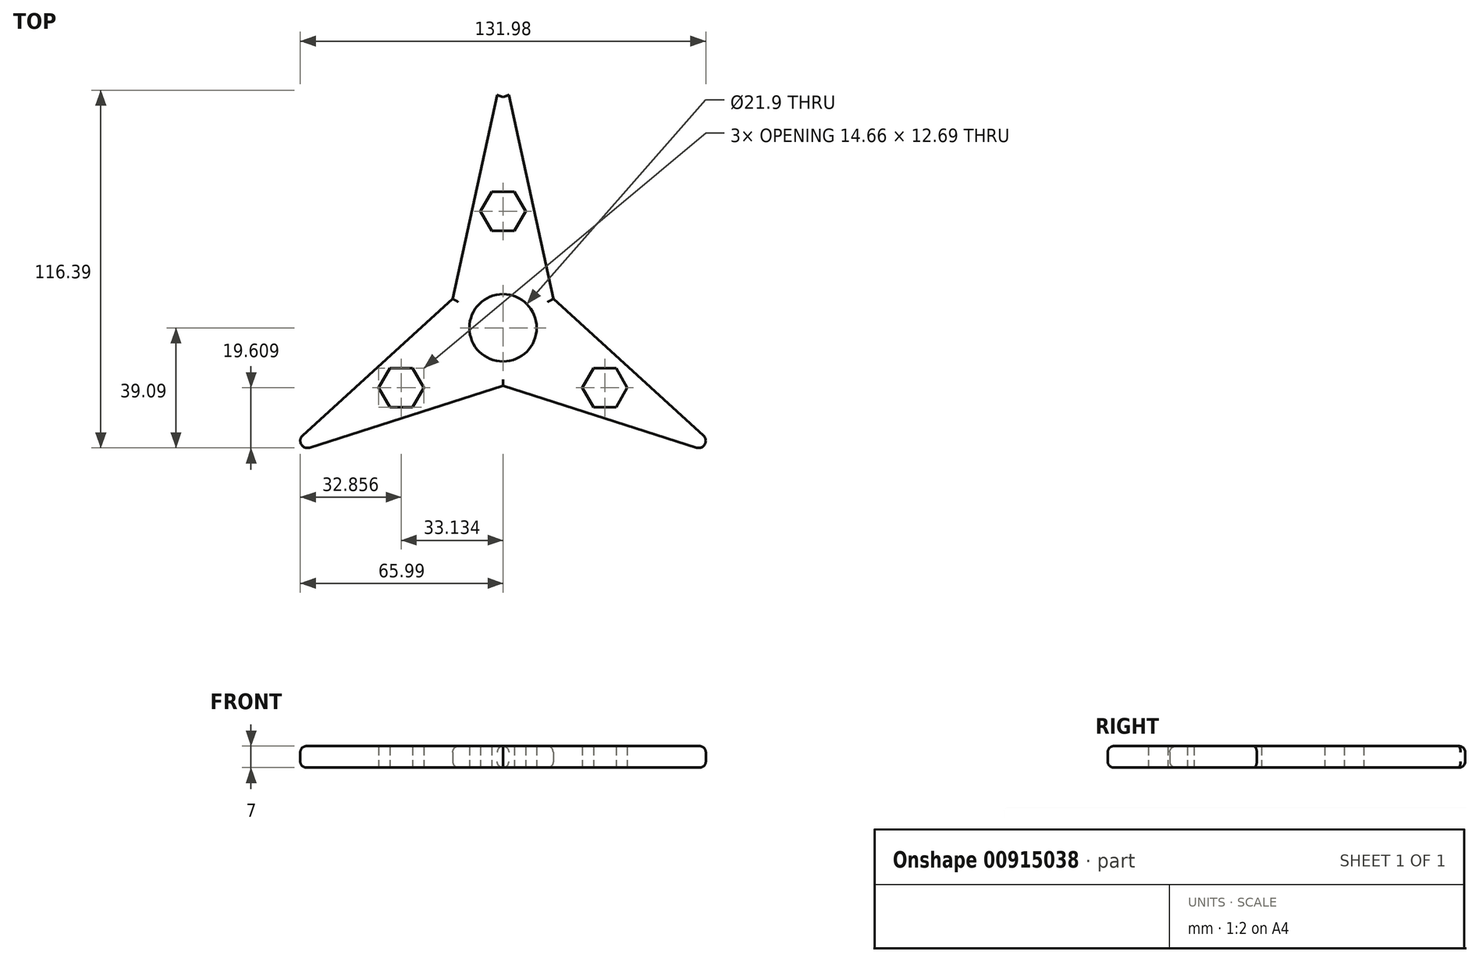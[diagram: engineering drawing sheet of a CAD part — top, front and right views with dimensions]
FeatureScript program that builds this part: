
annotation { "Feature Type Name" : "Feature", "Feature Type Description" : "" }
export const myFeature = defineFeature(function(context is Context, id is Id, definition is map)
    precondition{}
    {
        {
            var Q0;
            Q0=qCreatedBy(makeId("Top.planeOp"),FACE);
            var sketch = newSketch(context, id + "F0", { "sketchPlane" : qUnion([Q0])});
            skLineSegment(sketch, "E0", {"start": v(16.35, 9.44) * mm, "end": v(1.89, 75.78) * mm});
            skLineSegment(sketch, "E1", {"start": v(-1.89, 75.78) * mm, "end": v(-16.35, 9.44) * mm});
            skLineSegment(sketch, "E2.1.0", {"start": v(-62.96, -38.98) * mm, "end": v(0, -18.88) * mm});
            skLineSegment(sketch, "E2.1.1", {"start": v(-16.35, 9.44) * mm, "end": v(-65.23, -35.03) * mm});
            skLineSegment(sketch, "E2.2.0", {"start": v(65.23, -35.03) * mm, "end": v(16.35, 9.44) * mm});
            skLineSegment(sketch, "E2.2.1", {"start": v(0, -18.88) * mm, "end": v(62.96, -38.98) * mm});
            skCircle(sketch, "E3", {"center": v(0, 0) * mm, "radius": 10.95 * mm});
            skCircle(sketch, "E4.cCircle", {"center": v(0, 37.9) * mm, "radius": 6.35 * mm, "construction": true});
            skLineSegment(sketch, "E4.0", {"start": v(3.66, 31.56) * mm, "end": v(-3.66, 31.56) * mm});
            skLineSegment(sketch, "E4.1", {"start": v(-3.66, 31.56) * mm, "end": v(-7.33, 37.9) * mm});
            skLineSegment(sketch, "E4.2", {"start": v(-7.33, 37.9) * mm, "end": v(-3.66, 44.26) * mm});
            skLineSegment(sketch, "E4.3", {"start": v(-3.66, 44.26) * mm, "end": v(3.66, 44.26) * mm});
            skLineSegment(sketch, "E4.4", {"start": v(3.66, 44.26) * mm, "end": v(7.33, 37.9) * mm});
            skLineSegment(sketch, "E4.5", {"start": v(7.33, 37.9) * mm, "end": v(3.66, 31.56) * mm});
            skLineSegment(sketch, "E5.1.0", {"start": v(-36.8, -25.83) * mm, "end": v(-40.46, -19.48) * mm});
            skLineSegment(sketch, "E5.1.1", {"start": v(-29.47, -25.83) * mm, "end": v(-36.8, -25.83) * mm});
            skCircle(sketch, "E5.1.2", {"center": v(-33.13, -19.48) * mm, "radius": 6.35 * mm, "construction": true});
            skLineSegment(sketch, "E5.1.3", {"start": v(-40.46, -19.48) * mm, "end": v(-36.8, -13.13) * mm});
            skLineSegment(sketch, "E5.1.4", {"start": v(-36.8, -13.13) * mm, "end": v(-29.47, -13.13) * mm});
            skLineSegment(sketch, "E5.1.5", {"start": v(-25.8, -19.48) * mm, "end": v(-29.47, -25.83) * mm});
            skLineSegment(sketch, "E5.1.7", {"start": v(-29.47, -13.13) * mm, "end": v(-25.8, -19.48) * mm});
            skLineSegment(sketch, "E5.2.0", {"start": v(40.46, -19.48) * mm, "end": v(36.8, -25.83) * mm});
            skLineSegment(sketch, "E5.2.1", {"start": v(36.8, -13.13) * mm, "end": v(40.46, -19.48) * mm});
            skCircle(sketch, "E5.2.2", {"center": v(33.13, -19.48) * mm, "radius": 6.35 * mm, "construction": true});
            skLineSegment(sketch, "E5.2.3", {"start": v(36.8, -25.83) * mm, "end": v(29.47, -25.83) * mm});
            skLineSegment(sketch, "E5.2.4", {"start": v(29.47, -25.83) * mm, "end": v(25.8, -19.48) * mm});
            skLineSegment(sketch, "E5.2.5", {"start": v(29.47, -13.13) * mm, "end": v(36.8, -13.13) * mm});
            skLineSegment(sketch, "E5.2.7", {"start": v(25.8, -19.48) * mm, "end": v(29.47, -13.13) * mm});
            skPoint(sketch, "E5.center", {"position": v(0, -0.35) * mm});
            skArc(sketch, "E6.filletArc", {"start": v(62.96, -38.98) * mm, "mid": v(65.68, -37.92) * mm, "end": v(65.23, -35.03) * mm});
            skArc(sketch, "E7.filletArc", {"start": v(1.89, 75.78) * mm, "mid": v(0, 77.3) * mm, "end": v(-1.89, 75.78) * mm});
            skArc(sketch, "E8.filletArc", {"start": v(-65.23, -35.03) * mm, "mid": v(-65.68, -37.92) * mm, "end": v(-62.96, -38.98) * mm});
            skSolve(sketch);
        }
        {
            var Q0;
            Q0=qSketchRegion(id+"F0",true);
            extrude(context, id + "F1", {"entities" : qUnion([Q0]), "depth" : 7 * mm, "offsetDistance" : 25.4 * mm});
        }
        {
            var Q0;
            Q0=makeQuery(id+"F1.opExtrude","CAP_EDGE",EDGE,{"disambiguationData":[OSD([sQuery(id+"F0.wireOp",EDGE,"E1")])],"isStart":true});
            var Q1;
            Q1=makeQuery(id+"F1.opExtrude","CAP_EDGE",EDGE,{"disambiguationData":[OSD([sQuery(id+"F0.wireOp",EDGE,"E0")])],"isStart":true});
            fillet(context, id + "F2", {"entities" : qUnion([Q0, Q1]), "radius" : 2 * mm, "tangentPropagation" : true, "allowEdgeOverflow" : false});
        }
        {
            var Q0;
            Q0=makeQuery(id+"F1.opExtrude","CAP_EDGE",EDGE,{"disambiguationData":[OSD([sQuery(id+"F0.wireOp",EDGE,"E2.1.1")])],"isStart":true});
            var Q1;
            Q1=makeQuery(id+"F1.opExtrude","CAP_EDGE",EDGE,{"disambiguationData":[OSD([sQuery(id+"F0.wireOp",EDGE,"E2.1.0")])],"isStart":true});
            fillet(context, id + "F3", {"entities" : qUnion([Q0, Q1]), "radius" : 2 * mm, "tangentPropagation" : true, "allowEdgeOverflow" : false});
        }
        {
            var Q0;
            Q0=makeQuery(id+"F1.opExtrude","CAP_EDGE",EDGE,{"disambiguationData":[OSD([sQuery(id+"F0.wireOp",EDGE,"E2.2.1")])],"isStart":true});
            var Q1;
            Q1=makeQuery(id+"F1.opExtrude","CAP_EDGE",EDGE,{"disambiguationData":[OSD([sQuery(id+"F0.wireOp",EDGE,"E2.2.0")])],"isStart":true});
            fillet(context, id + "F4", {"entities" : qUnion([Q0, Q1]), "radius" : 2 * mm, "tangentPropagation" : true, "allowEdgeOverflow" : false});
        }
        {
            var Q0;
            Q0=makeQuery(id+"F1.opExtrude","CAP_EDGE",EDGE,{"disambiguationData":[OSD([sQuery(id+"F0.wireOp",EDGE,"E2.2.0")])],"isStart":false});
            fillet(context, id + "F5", {"entities" : qUnion([Q0]), "radius" : 2 * mm, "tangentPropagation" : true, "allowEdgeOverflow" : false});
        }
        {
            var Q0;
            Q0=makeQuery(id+"F1.opExtrude","CAP_EDGE",EDGE,{"disambiguationData":[OSD([sQuery(id+"F0.wireOp",EDGE,"E2.1.1")])],"isStart":false});
            fillet(context, id + "F6", {"entities" : qUnion([Q0]), "radius" : 2 * mm, "tangentPropagation" : true, "allowEdgeOverflow" : false});
        }
        {
            var Q0;
            Q0=makeQuery(id+"F1.opExtrude","CAP_EDGE",EDGE,{"disambiguationData":[OSD([sQuery(id+"F0.wireOp",EDGE,"E1")])],"isStart":false});
            fillet(context, id + "F7", {"entities" : qUnion([Q0]), "radius" : 2 * mm, "tangentPropagation" : true, "allowEdgeOverflow" : false});
        }
    });
